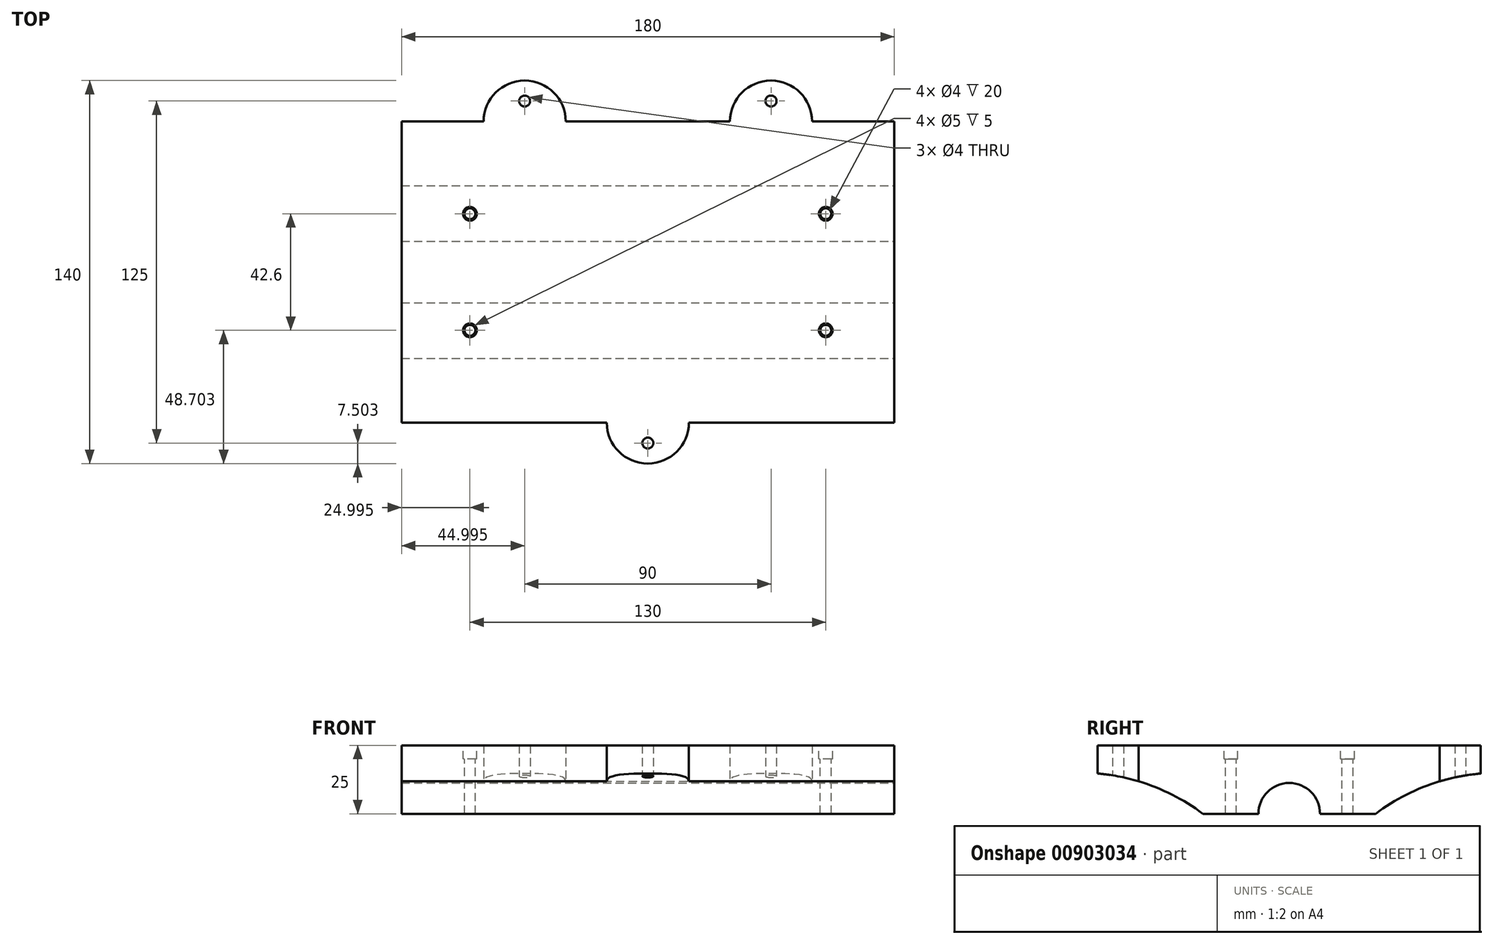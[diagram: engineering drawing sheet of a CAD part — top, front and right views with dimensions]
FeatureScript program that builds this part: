
annotation { "Feature Type Name" : "Feature", "Feature Type Description" : "" }
export const myFeature = defineFeature(function(context is Context, id is Id, definition is map)
    precondition{}
    {
        {
            var Q0;
            Q0=qCreatedBy(makeId("Top.planeOp"),FACE);
            var sketch = newSketch(context, id + "F0", { "sketchPlane" : qUnion([Q0])});
            skLineSegment(sketch, "E0.bottom", {"start": v(-81.43, 66.57) * mm, "end": v(-51.43, 66.57) * mm});
            skLineSegment(sketch, "E0.top", {"start": v(-81.43, -43.43) * mm, "end": v(-6.43, -43.43) * mm});
            skLineSegment(sketch, "E0.left", {"start": v(-81.43, 66.57) * mm, "end": v(-81.43, -43.43) * mm});
            skLineSegment(sketch, "E0.right", {"start": v(98.57, 66.57) * mm, "end": v(98.57, -43.43) * mm});
            skLineSegment(sketch, "E1", {"start": v(-81.43, 96.12) * mm, "end": v(8.57, 96.12) * mm, "construction": true});
            skPoint(sketch, "E1.endSnap0", {"position": v(8.57, 66.57) * mm});
            skLineSegment(sketch, "E2", {"start": v(8.57, 96.12) * mm, "end": v(98.57, 96.12) * mm, "construction": true});
            skLineSegment(sketch, "E3", {"start": v(-36.43, 81.57) * mm, "end": v(-36.43, 66.57) * mm, "construction": true});
            skLineSegment(sketch, "E4", {"start": v(53.57, 81.57) * mm, "end": v(53.57, 66.57) * mm, "construction": true});
            skArc(sketch, "E5", {"start": v(-21.43, 66.57) * mm, "mid": v(-36.43, 81.57) * mm, "end": v(-51.43, 66.57) * mm});
            skArc(sketch, "E6", {"start": v(68.57, 66.57) * mm, "mid": v(53.57, 81.57) * mm, "end": v(38.57, 66.57) * mm});
            skArc(sketch, "E7", {"start": v(-6.43, -43.43) * mm, "mid": v(8.57, -58.43) * mm, "end": v(23.57, -43.43) * mm});
            skLineSegment(sketch, "E8.trimOffspring", {"start": v(23.57, -43.43) * mm, "end": v(98.57, -43.43) * mm});
            skLineSegment(sketch, "E9.trimOffspring", {"start": v(-21.43, 66.57) * mm, "end": v(38.57, 66.57) * mm});
            skLineSegment(sketch, "E10.trimOffspring", {"start": v(68.57, 66.57) * mm, "end": v(98.57, 66.57) * mm});
            skPoint(sketch, "E11.orphan", {"position": v(53.57, 96.12) * mm});
            skPoint(sketch, "E12.orphan", {"position": v(-36.43, 96.12) * mm});
            skLineSegment(sketch, "E13", {"start": v(53.57, 74.07) * mm, "end": v(-36.43, 74.07) * mm, "construction": true});
            skLineSegment(sketch, "E14", {"start": v(8.57, -58.43) * mm, "end": v(8.57, -43.43) * mm, "construction": true});
            skCircle(sketch, "E15", {"center": v(8.57, -50.93) * mm, "radius": 2 * mm});
            skCircle(sketch, "E16", {"center": v(53.57, 74.07) * mm, "radius": 2 * mm});
            skCircle(sketch, "E17", {"center": v(-36.43, 74.07) * mm, "radius": 2 * mm});
            skSolve(sketch);
        }
        {
            var Q0;
            Q0 = qSketchRegion(id + "F0", true);
            extrude(context, id + "F1", {"entities" : qUnion([Q0]), "depth" : 25 * mm, "offsetDistance" : 25 * mm});
        }
        {
            var Q0;
            Q0=makeQuery(id+"F1.opExtrude","SWEPT_FACE",FACE,{"disambiguationData":[OSD([sQuery(id+"F0.wireOp",EDGE,"E0.right")])]});
            var sketch = newSketch(context, id + "F2", { "sketchPlane" : qUnion([Q0])});
            skArc(sketch, "E18", {"start": v(22.82, 0) * mm, "mid": v(11.57, 11.25) * mm, "end": v(0.32, 0) * mm});
            skLineSegment(sketch, "E19", {"start": v(-64.9, 25) * mm, "end": v(-64.9, 15) * mm, "construction": true});
            skLineSegment(sketch, "E20", {"start": v(-64.9, 15) * mm, "end": v(92.3, 15) * mm, "construction": true});
            skArc(sketch, "E21", {"start": v(-20, 0) * mm, "mid": v(-41.23, 11.15) * mm, "end": v(-64.9, 15) * mm});
            skLineSegment(sketch, "E22", {"start": v(11.57, 0) * mm, "end": v(11.57, -67.92) * mm, "construction": true});
            skArc(sketch, "E23.MirrorCS", {"start": v(43.15, 0) * mm, "mid": v(64.38, 11.15) * mm, "end": v(88.05, 15) * mm});
            skLineSegment(sketch, "E24", {"start": v(88.05, 15) * mm, "end": v(88.05, -16.41) * mm});
            skLineSegment(sketch, "E25", {"start": v(88.05, -16.41) * mm, "end": v(-64.9, -16.41) * mm});
            skLineSegment(sketch, "E26", {"start": v(-64.9, -16.41) * mm, "end": v(-64.9, 15) * mm});
            skLineSegment(sketch, "E27", {"start": v(-20, 0) * mm, "end": v(0.32, 0) * mm});
            skLineSegment(sketch, "E28.MirrorCS", {"start": v(43.15, 0) * mm, "end": v(22.82, 0) * mm});
            skSolve(sketch);
        }
        {
            var Q0;
            Q0 = qSketchRegion(id + "F2", true);
            extrude(context, id + "F3", {"entities" : qUnion([Q0]), "operationType" : NewBodyOperationType.REMOVE, "oppositeDirection" : true, "depth" : 276 * mm, "offsetDistance" : 25 * mm});
        }
        {
            var Q0;
            Q0=makeQuery(id+"F1.opExtrude","CAP_FACE",FACE,{"disambiguationData":[OSD([sQuery(id+"F0.wireOp",EDGE,"E0.bottom"),sQuery(id+"F0.wireOp",EDGE,"E0.top"),sQuery(id+"F0.wireOp",EDGE,"E0.left"),sQuery(id+"F0.wireOp",EDGE,"E0.right"),sQuery(id+"F0.wireOp",EDGE,"E5"),sQuery(id+"F0.wireOp",EDGE,"E6"),sQuery(id+"F0.wireOp",EDGE,"E7"),sQuery(id+"F0.wireOp",EDGE,"E8.trimOffspring"),sQuery(id+"F0.wireOp",EDGE,"E9.trimOffspring"),sQuery(id+"F0.wireOp",EDGE,"E10.trimOffspring"),sQuery(id+"F0.wireOp",EDGE,"E15"),sQuery(id+"F0.wireOp",EDGE,"E16"),sQuery(id+"F0.wireOp",EDGE,"E17")])],"isStart":false});
            var sketch = newSketch(context, id + "F4", { "sketchPlane" : qUnion([Q0])});
            skLineSegment(sketch, "E29", {"start": v(-66.43, 11.57) * mm, "end": v(83.57, 11.57) * mm, "construction": true});
            skPoint(sketch, "E30", {"position": v(63.57, 11.57) * mm});
            skPoint(sketch, "E31", {"position": v(-46.43, 11.57) * mm});
            skLineSegment(sketch, "E32", {"start": v(-66.43, 11.57) * mm, "end": v(-46.43, 11.57) * mm, "construction": true});
            skLineSegment(sketch, "E33", {"start": v(63.57, 11.57) * mm, "end": v(83.57, 11.57) * mm, "construction": true});
            skLineSegment(sketch, "E34", {"start": v(-56.43, 11.57) * mm, "end": v(-56.43, 22.87) * mm, "construction": true});
            skLineSegment(sketch, "E35", {"start": v(73.57, 11.57) * mm, "end": v(73.57, 22.87) * mm, "construction": true});
            skLineSegment(sketch, "E36", {"start": v(-56.43, 22.87) * mm, "end": v(-56.43, 42.87) * mm, "construction": true});
            skLineSegment(sketch, "E37", {"start": v(73.57, 22.87) * mm, "end": v(73.57, 42.87) * mm, "construction": true});
            skCircle(sketch, "E38", {"center": v(-56.43, 32.87) * mm, "radius": 2 * mm});
            skCircle(sketch, "E39", {"center": v(73.57, 32.87) * mm, "radius": 2 * mm});
            skLineSegment(sketch, "E40", {"start": v(-81.43, 11.57) * mm, "end": v(98.57, 11.57) * mm, "construction": true});
            skCircle(sketch, "E41.MirrorC", {"center": v(-56.43, -9.73) * mm, "radius": 2 * mm});
            skCircle(sketch, "E42.MirrorC", {"center": v(73.57, -9.73) * mm, "radius": 2 * mm});
            skPoint(sketch, "E43", {"position": v(8.57, 11.57) * mm});
            skSolve(sketch);
        }
        {
            var Q0;
            Q0 = qSketchRegion(id + "F4", true);
            extrude(context, id + "F5", {"entities" : qUnion([Q0]), "operationType" : NewBodyOperationType.REMOVE, "oppositeDirection" : true, "depth" : 84.8 * mm, "offsetDistance" : 25 * mm});
        }
        {
            var Q0;
            Q0=makeQuery(id+"F1.opExtrude","CAP_FACE",FACE,{"disambiguationData":[OSD([sQuery(id+"F0.wireOp",EDGE,"E0.bottom"),sQuery(id+"F0.wireOp",EDGE,"E0.top"),sQuery(id+"F0.wireOp",EDGE,"E0.left"),sQuery(id+"F0.wireOp",EDGE,"E0.right"),sQuery(id+"F0.wireOp",EDGE,"E5"),sQuery(id+"F0.wireOp",EDGE,"E6"),sQuery(id+"F0.wireOp",EDGE,"E7"),sQuery(id+"F0.wireOp",EDGE,"E8.trimOffspring"),sQuery(id+"F0.wireOp",EDGE,"E9.trimOffspring"),sQuery(id+"F0.wireOp",EDGE,"E10.trimOffspring"),sQuery(id+"F0.wireOp",EDGE,"E15"),sQuery(id+"F0.wireOp",EDGE,"E16"),sQuery(id+"F0.wireOp",EDGE,"E17")])],"isStart":false});
            var sketch = newSketch(context, id + "F6", { "sketchPlane" : qUnion([Q0])});
            skCircle(sketch, "E44", {"center": v(-56.43, 32.87) * mm, "radius": 2.5 * mm});
            skCircle(sketch, "E45", {"center": v(73.57, 32.87) * mm, "radius": 2.5 * mm});
            skCircle(sketch, "E46", {"center": v(73.57, -9.73) * mm, "radius": 2.5 * mm});
            skCircle(sketch, "E47", {"center": v(-56.43, -9.73) * mm, "radius": 2.5 * mm});
            skSolve(sketch);
        }
        {
            var Q0;
            Q0 = qSketchRegion(id + "F6", true);
            extrude(context, id + "F7", {"entities" : qUnion([Q0]), "operationType" : NewBodyOperationType.REMOVE, "oppositeDirection" : true, "depth" : 5 * mm, "offsetDistance" : 25 * mm});
        }
    });
